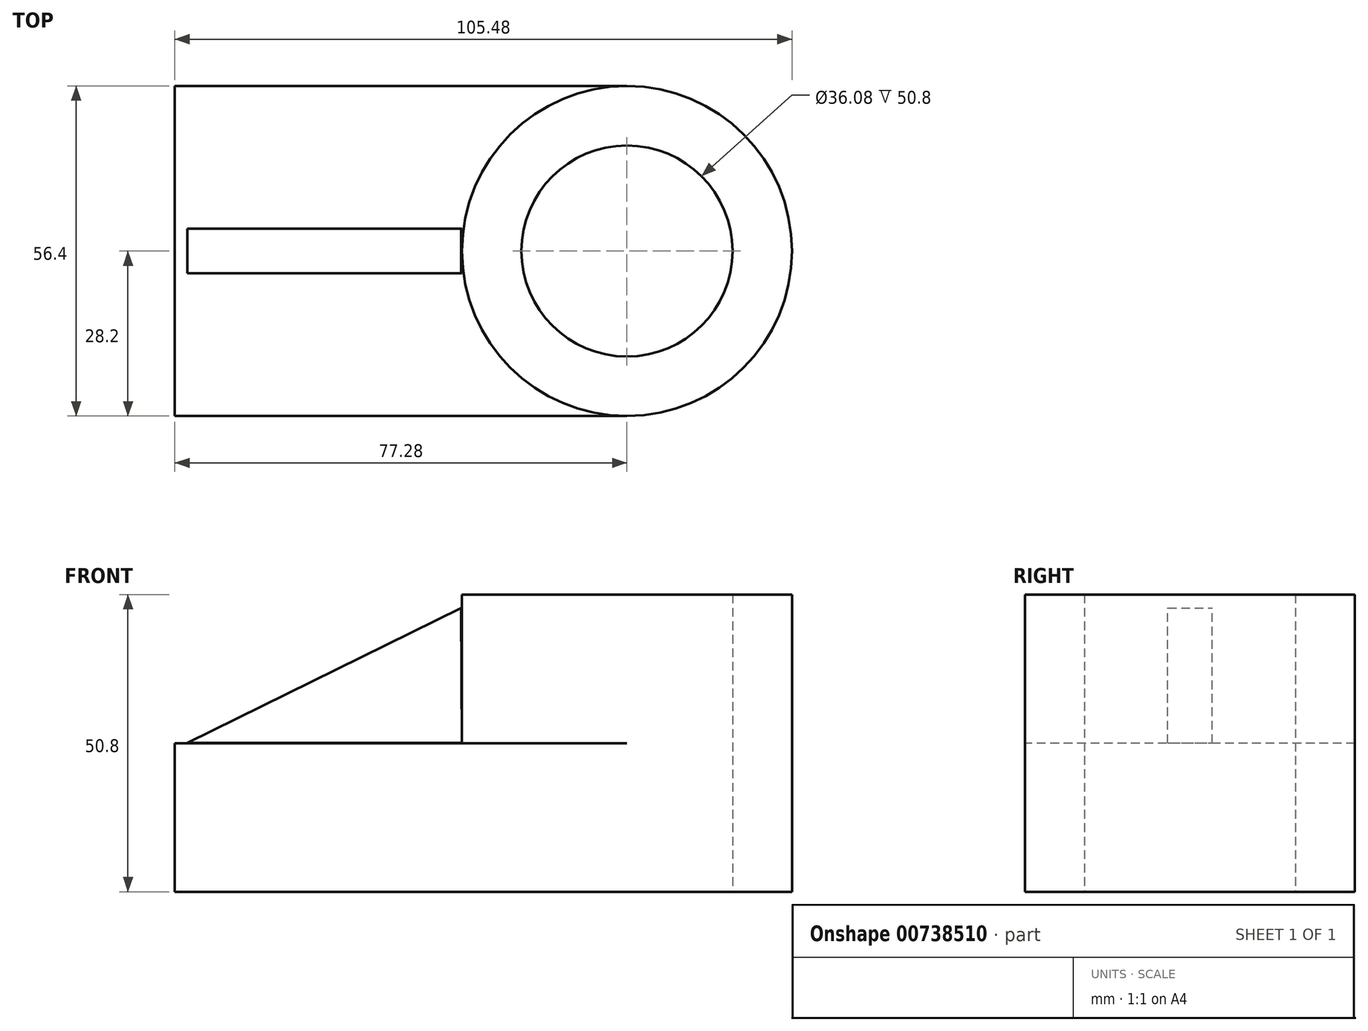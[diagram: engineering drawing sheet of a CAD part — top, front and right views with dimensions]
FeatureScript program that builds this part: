
annotation { "Feature Type Name" : "Feature", "Feature Type Description" : "" }
export const myFeature = defineFeature(function(context is Context, id is Id, definition is map)
    precondition{}
    {
        {
            var Q0;
            Q0=qCreatedBy(makeId("Top.planeOp"),FACE);
            var sketch = newSketch(context, id + "F0", { "sketchPlane" : qUnion([Q0])});
            skCircle(sketch, "E0", {"center": v(0, 0) * mm, "radius": 28.2 * mm});
            skCircle(sketch, "E1", {"center": v(0, 0) * mm, "radius": 18.04 * mm});
            skSolve(sketch);
        }
        {
            var Q0;
            Q0=makeQuery(id+"F0.imprint","IMPRINT",FACE,{"disambiguationData":[TD([[makeQuery(id+"F0.imprint","IMPRINT",EDGE,{"derivedFrom":sQuery(id+"F0.wireOp",EDGE,"E0")}),1.0]])]});
            extrude(context, id + "F1", {"entities" : qUnion([Q0]), "depth" : 50.8 * mm, "offsetDistance" : 25.4 * mm});
        }
        {
            var Q0;
            Q0=makeQuery(id+"F1.opExtrude","CAP_FACE",FACE,{"disambiguationData":[OSD([sQuery(id+"F0.wireOp",EDGE,"E0"),sQuery(id+"F0.wireOp",EDGE,"E1")])],"isStart":true});
            var sketch = newSketch(context, id + "F2", { "sketchPlane" : qUnion([Q0])});
            skLineSegment(sketch, "E2", {"start": v(0, -28.2) * mm, "end": v(-77.28, -28.2) * mm});
            skLineSegment(sketch, "E3", {"start": v(-77.28, -28.2) * mm, "end": v(-77.28, 28.2) * mm});
            skLineSegment(sketch, "E4", {"start": v(-77.28, 28.2) * mm, "end": v(0, 28.2) * mm});
            skSolve(sketch);
        }
        {
            var Q0;
            {var subQ0=sQuery(id+"F2.wireOp",EDGE,"E2");Q0=makeQuery(id+"F2.imprint","IMPRINT",FACE,{"disambiguationData":[TD([[makeQuery(id+"F2.imprint","IMPRINT",EDGE,{"derivedFrom":subQ0}),-1.0]])]});}
            extrude(context, id + "F3", {"entities" : qUnion([Q0]), "operationType" : NewBodyOperationType.ADD, "oppositeDirection" : true, "depth" : 25.4 * mm, "offsetDistance" : 25.4 * mm});
        }
        {
            var Q0;
            Q0=qCreatedBy(makeId("Front.planeOp"),FACE);
            var sketch = newSketch(context, id + "F4", { "sketchPlane" : qUnion([Q0])});
            skLineSegment(sketch, "E5", {"start": v(-28.36, 48.51) * mm, "end": v(-75.12, 25.41) * mm});
            skLineSegment(sketch, "E6", {"start": v(-75.12, 25.41) * mm, "end": v(-28.25, 25.41) * mm});
            skLineSegment(sketch, "E7", {"start": v(-28.25, 25.41) * mm, "end": v(-28.36, 48.51) * mm});
            skSolve(sketch);
        }
        {
            var Q0;
            Q0=makeQuery(id+"F4.imprint","IMPRINT",FACE,{"disambiguationData":[TD([[makeQuery(id+"F4.imprint","IMPRINT",EDGE,{"derivedFrom":sQuery(id+"F4.wireOp",EDGE,"E5")}),1.0]])]});
            extrude(context, id + "F5", {"entities" : qUnion([Q0]), "operationType" : NewBodyOperationType.ADD, "depth" : 7.62 * mm, "offsetDistance" : 25.4 * mm, "symmetric" : true});
        }
    });
